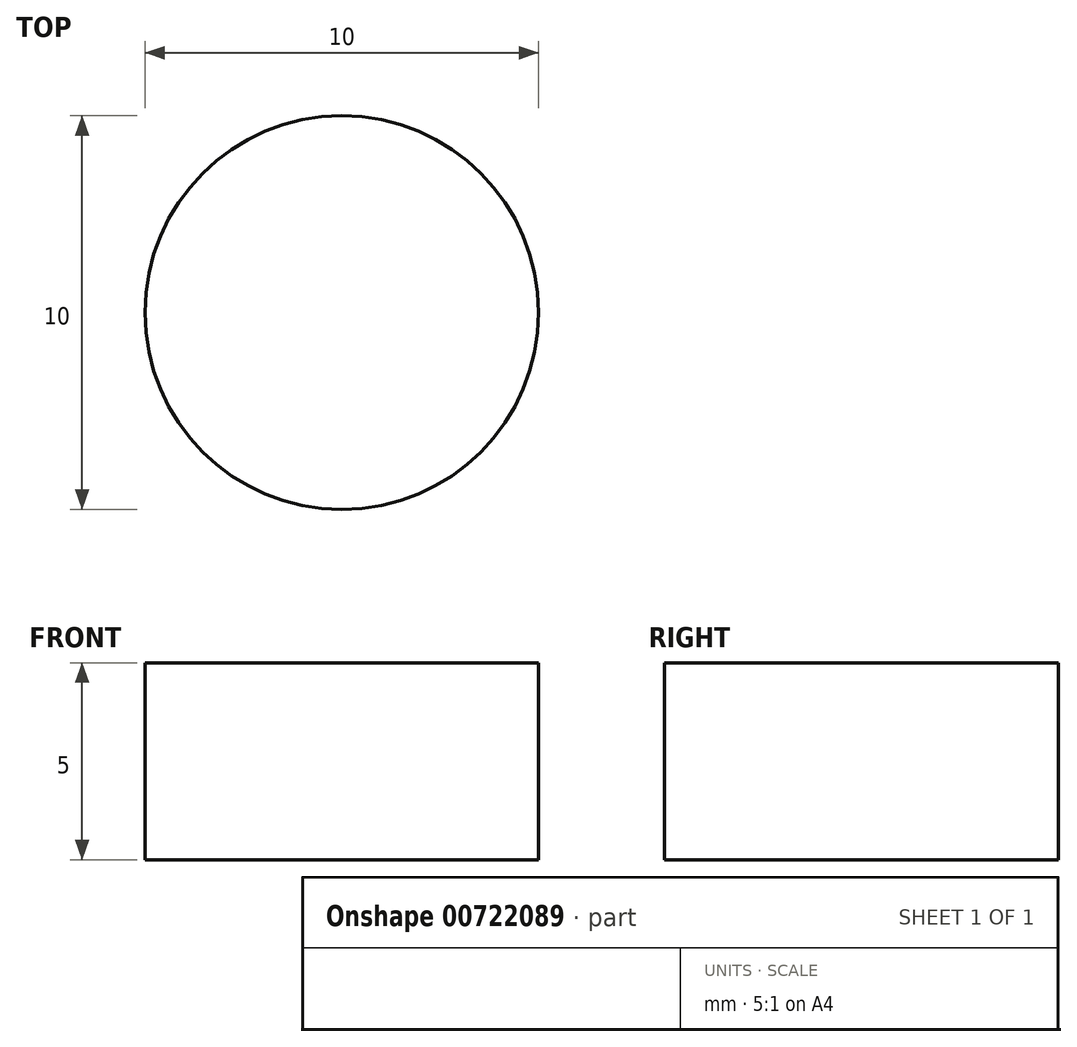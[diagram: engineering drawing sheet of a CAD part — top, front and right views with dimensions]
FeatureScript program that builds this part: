
annotation { "Feature Type Name" : "Feature", "Feature Type Description" : "" }
export const myFeature = defineFeature(function(context is Context, id is Id, definition is map)
    precondition{}
    {
        {
            var Q0;
            Q0=qCreatedBy(makeId("Top.planeOp"),FACE);
            var sketch = newSketch(context, id + "F0", { "sketchPlane" : qUnion([Q0])});
            skCircle(sketch, "E0", {"center": v(0, 0) * mm, "radius": 5 * mm});
            skSolve(sketch);
        }
        {
            var Q0;
            Q0=makeQuery(id+"F0.imprint","IMPRINT",FACE,{"disambiguationData":[TD([[makeQuery(id+"F0.imprint","IMPRINT",EDGE,{"derivedFrom":sQuery(id+"F0.wireOp",EDGE,"E0")}),1.0]])]});
            var Q1;
            Q1=sQuery(id+"F0.wireOp",EDGE,"E0");
            extrude(context, id + "F1", {"entities" : qUnion([Q0]), "surfaceEntities" : qUnion([Q1]), "depth" : 5 * mm, "offsetDistance" : 25 * mm});
        }
    });
